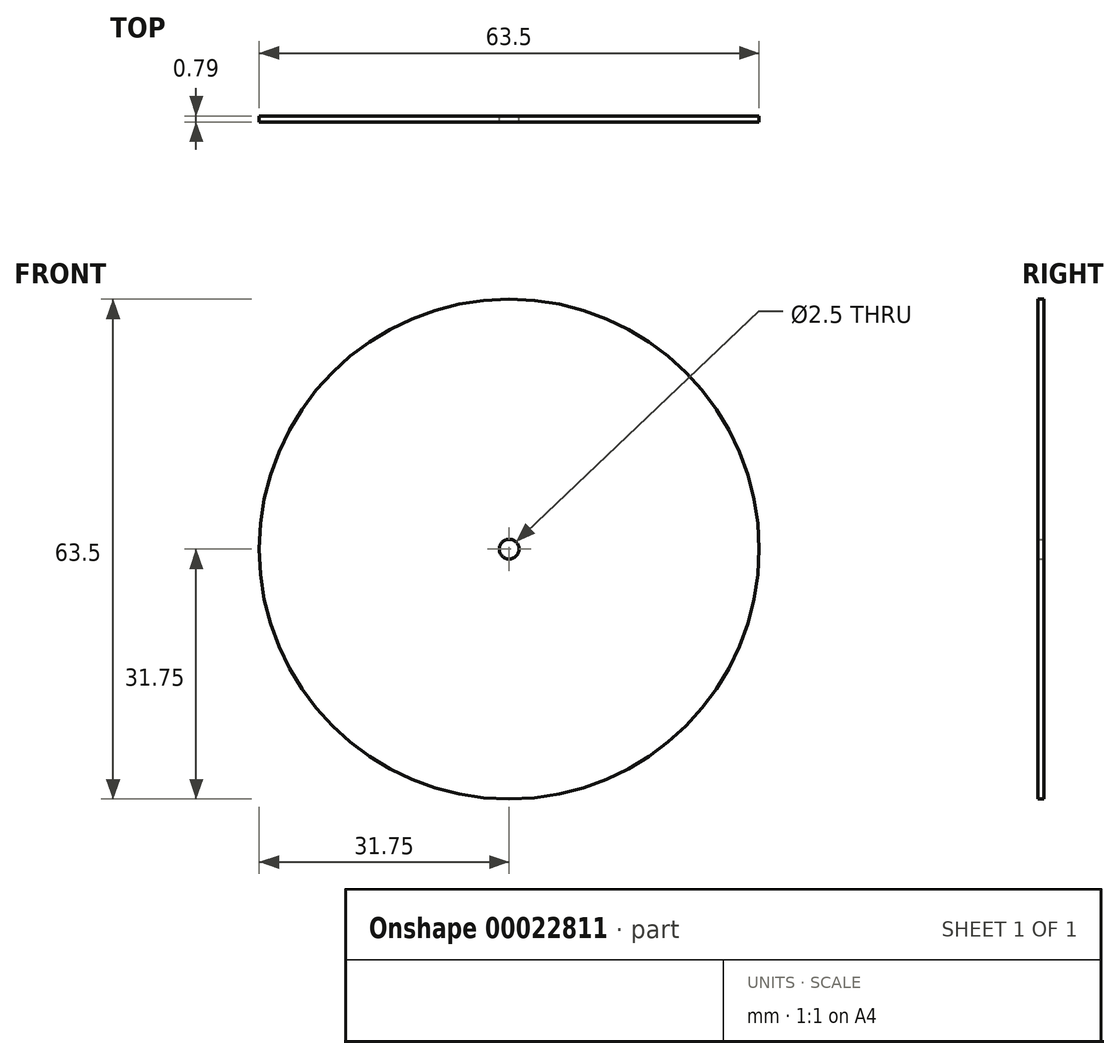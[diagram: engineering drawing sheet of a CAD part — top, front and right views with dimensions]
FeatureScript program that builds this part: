
annotation { "Feature Type Name" : "Feature", "Feature Type Description" : "" }
export const myFeature = defineFeature(function(context is Context, id is Id, definition is map)
    precondition{}
    {
        {
            var Q0;
            Q0=qCreatedBy(makeId("Front.planeOp"),FACE);
            var sketch = newSketch(context, id + "F0", { "sketchPlane" : qUnion([Q0])});
            skCircle(sketch, "E0", {"center": v(0, 0) * mm, "radius": 31.75 * mm});
            skCircle(sketch, "E1", {"center": v(0, 0) * mm, "radius": 1.25 * mm});
            skSolve(sketch);
        }
        {
            var Q0;
            Q0=makeQuery(id+"F0.imprint","IMPRINT",FACE,{"disambiguationData":[TD([[makeQuery(id+"F0.imprint","IMPRINT",EDGE,{"derivedFrom":sQuery(id+"F0.wireOp",EDGE,"E0")}),1.0]])]});
            extrude(context, id + "F1", {"entities" : qUnion([Q0]), "depth" : 0.8 * mm});
        }
    });
